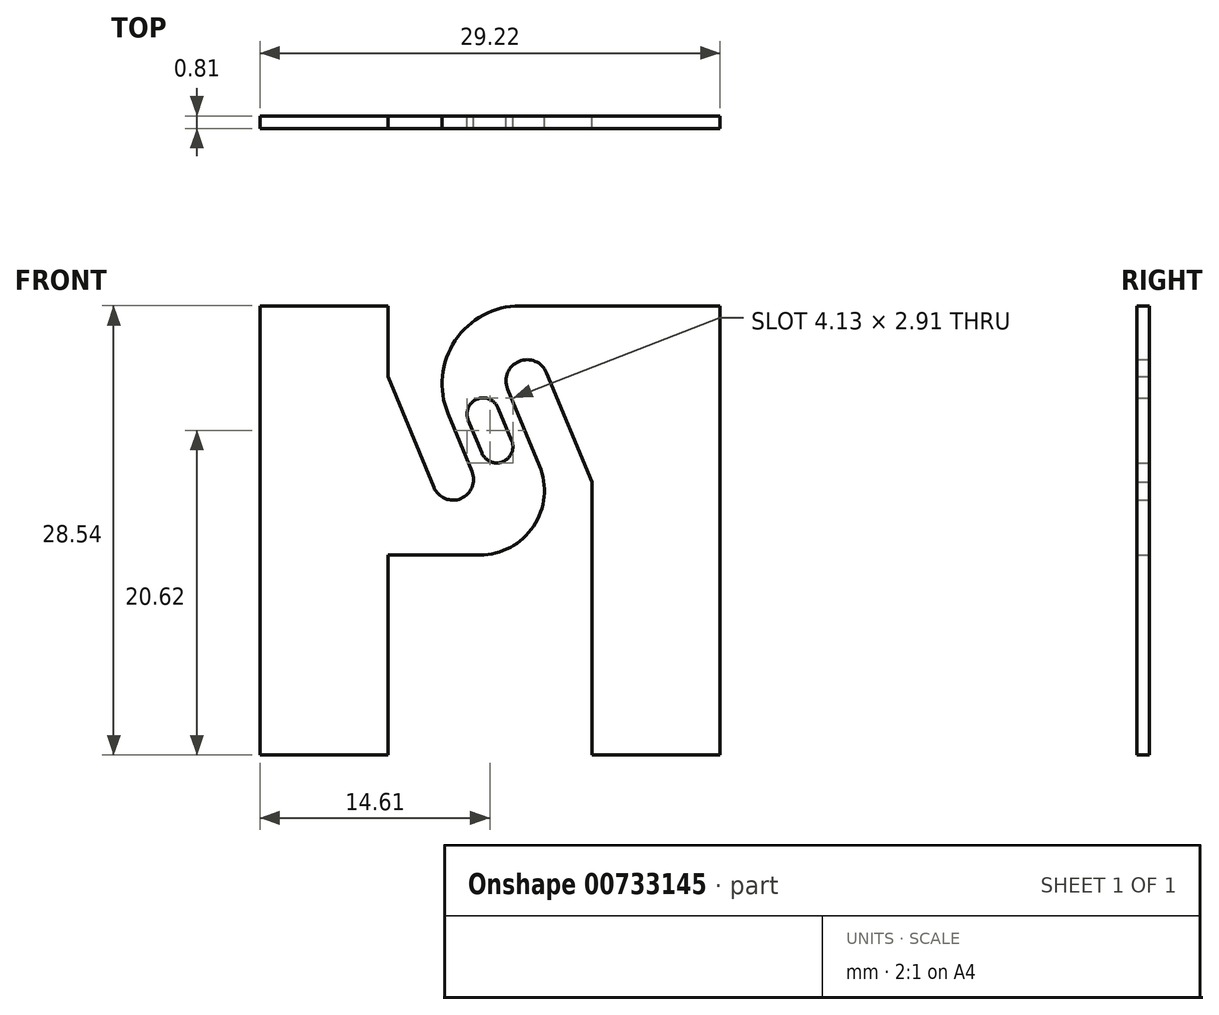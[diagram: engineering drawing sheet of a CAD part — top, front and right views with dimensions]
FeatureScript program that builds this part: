
annotation { "Feature Type Name" : "Feature", "Feature Type Description" : "" }
export const myFeature = defineFeature(function(context is Context, id is Id, definition is map)
    precondition{}
    {
        {
            var Q0;
            Q0=qCreatedBy(makeId("Front.planeOp"),FACE);
            var sketch = newSketch(context, id + "F0", { "sketchPlane" : qUnion([Q0])});
            skLineSegment(sketch, "E0.left", {"start": v(-1.38, 0.65) * mm, "end": v(-0.52, -1.43) * mm});
            skLineSegment(sketch, "E0.right", {"start": v(0.52, 1.43) * mm, "end": v(1.38, -0.65) * mm});
            skPoint(sketch, "E0.middle", {"position": v(0, 0) * mm});
            skLineSegment(sketch, "E1", {"start": v(0, 0) * mm, "end": v(0.53, 0) * mm, "construction": true});
            skArc(sketch, "E2", {"start": v(-1.38, 0.65) * mm, "mid": v(-0.82, 1.99) * mm, "end": v(0.52, 1.43) * mm});
            skArc(sketch, "E3", {"start": v(1.38, -0.65) * mm, "mid": v(0.82, -1.99) * mm, "end": v(-0.52, -1.43) * mm});
            skLineSegment(sketch, "E4", {"start": v(-0.43, 1.04) * mm, "end": v(0, 0) * mm});
            skLineSegment(sketch, "E5", {"start": v(0.43, -1.04) * mm, "end": v(0, 0) * mm});
            skLineSegment(sketch, "E6.bottom", {"start": v(-6.47, 7.92) * mm, "end": v(-14.6, 7.92) * mm});
            skLineSegment(sketch, "E6.left", {"start": v(-6.47, 7.91) * mm, "end": v(-6.47, 3.41) * mm});
            skLineSegment(sketch, "E6.right", {"start": v(-14.6, 7.92) * mm, "end": v(-14.6, -7.92) * mm});
            skLineSegment(sketch, "E7.top", {"start": v(-6.47, -20.61) * mm, "end": v(-14.6, -20.61) * mm});
            skLineSegment(sketch, "E7.left", {"start": v(-6.48, -7.92) * mm, "end": v(-6.47, -20.61) * mm});
            skLineSegment(sketch, "E7.right", {"start": v(-14.6, -7.92) * mm, "end": v(-14.6, -20.61) * mm});
            skLineSegment(sketch, "E8.bottom", {"start": v(6.47, 7.92) * mm, "end": v(14.6, 7.92) * mm});
            skLineSegment(sketch, "E8.left", {"start": v(6.47, -3.27) * mm, "end": v(6.47, -7.92) * mm});
            skLineSegment(sketch, "E8.right", {"start": v(14.6, 7.92) * mm, "end": v(14.6, -7.91) * mm});
            skLineSegment(sketch, "E9.top", {"start": v(14.6, -20.61) * mm, "end": v(6.48, -20.61) * mm});
            skLineSegment(sketch, "E9.left", {"start": v(14.6, -7.91) * mm, "end": v(14.6, -20.61) * mm});
            skLineSegment(sketch, "E9.right", {"start": v(6.47, -7.92) * mm, "end": v(6.48, -20.61) * mm});
            skLineSegment(sketch, "E10", {"start": v(-6.48, -7.91) * mm, "end": v(-0.64, -7.91) * mm});
            skArc(sketch, "E11", {"start": v(-0.64, -7.92) * mm, "mid": v(2.77, -6.1) * mm, "end": v(3.15, -2.25) * mm});
            skLineSegment(sketch, "E12", {"start": v(-2.66, 1.07) * mm, "end": v(-1.14, -2.61) * mm});
            skArc(sketch, "E13", {"start": v(1.13, 2.64) * mm, "mid": v(1.85, 4.39) * mm, "end": v(3.6, 3.66) * mm});
            skLineSegment(sketch, "E14", {"start": v(3.6, 3.66) * mm, "end": v(6.47, -3.27) * mm});
            skArc(sketch, "E15", {"start": v(-1.14, -2.61) * mm, "mid": v(-1.85, -4.33) * mm, "end": v(-3.56, -3.62) * mm});
            skLineSegment(sketch, "E16", {"start": v(-3.56, -3.62) * mm, "end": v(-6.48, 3.41) * mm});
            skLineSegment(sketch, "E17", {"start": v(1.13, 2.64) * mm, "end": v(3.15, -2.25) * mm});
            skLineSegment(sketch, "E18", {"start": v(6.47, 7.92) * mm, "end": v(1.91, 7.92) * mm});
            skPoint(sketch, "E19.endSnap0", {"position": v(-0.82, 1.99) * mm});
            skArc(sketch, "E20", {"start": v(1.91, 7.92) * mm, "mid": v(-2.2, 5.71) * mm, "end": v(-2.66, 1.07) * mm});
            skSolve(sketch);
        }
        {
            var Q0;
            Q0=makeQuery(id+"F0.imprint","IMPRINT",FACE,{"disambiguationData":[TD([[makeQuery(id+"F0.imprint","IMPRINT",EDGE,{"derivedFrom":sQuery(id+"F0.wireOp",EDGE,"E0.left")}),-1.0]])]});
            extrude(context, id + "F1", {"entities" : qUnion([Q0]), "depth" : 0.81 * mm, "offsetDistance" : 25 * mm});
        }
    });
